# Revit family: Caroma Liano EH CF Invisi Suite
name_source: partatom
category: Plumbing Fixtures
revit_build: Autodesk Revit LT 2016 (Build: 20151007_0715(x64)
units: mm (PartAtom-declared; Revit-internal decimal feet)

## family parameters
Cut with Voids When Loaded = Yes
Host = Face
OmniClass Number = 23.45.05.21.11.11
OmniClass Title = Water Operated Water Closets
Part Type = Normal
Room Calculation Point = No
Round Connector Dimension = Use Diameter
Shared = No

## types (1)
- Liano
    Assembly Code = D2010110
    CW Connection = Yes
    CWFU = 2
    Default Elevation = 0 mm  [stored 0 ft]
    Description = Liano Easy Height Vitreous China Wall Faced Pan and Invisi II Smartflush Cistern
    HW Connection = No
    Hardware = Metal-Chrome-Caroma
    Keynote = WC
    Manufacturer = Caroma
    Material_ANZRS = Porcelain-White-Caroma
    Model = 766350W
    Type Comments = Liano Easy Height Cleanflush Toilet Suite with Back Inlet Pan, Internal Overflow Cistern and Seat
    URL = www.caroma.com.au
    Vent Connection = No
    WELSRating_ANZRS = 4
    WFU = 3
    Waste Connection = Yes

note: [stored X ft] marks values corroborated as IEEE doubles in the binary element streams (Revit-internal decimal feet)

## geometry (parser evidence)
native form markers: Blend x8, Sweep x2
no freeform markers — native parametric forms only
